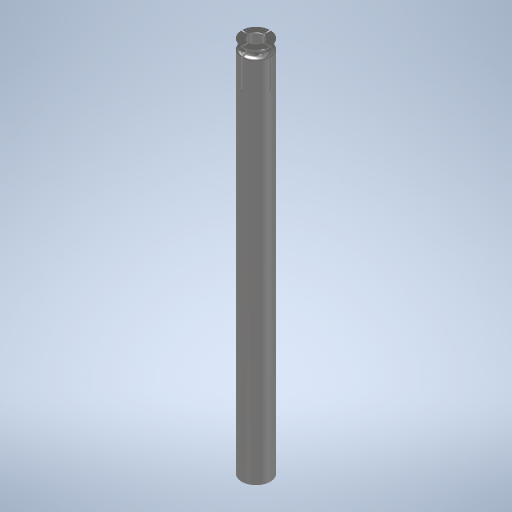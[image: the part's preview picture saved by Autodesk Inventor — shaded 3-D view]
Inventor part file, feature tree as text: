
AUTODESK INVENTOR PART (.ipt)
format: ipt  version: 2023.2 (Build 272271000, 271)  size: 301,056 bytes
history: native  units: mm
features: sketch x6, extrude x5, plane x1, hole x1, chamfer x1, revolve x1
ambient origin geometry x8: Origin, YZ Plane, XZ Plane, XY Plane, X Axis, Y Axis, Z Axis, Center Point
bodies: Volumenkörper1 (feature_tree)
feature tree (15):
  extrude  "Extrusion1"  Depth=6.0mm
  extrude  "Extrusion2"  Depth=8.0mm TaperAngle=0.0deg
  extrude  "Extrusion3"  Depth=3.0mm
  plane  "Arbeitsebene1"
  extrude  "Extrusion4"  Depth=1.0mm TaperAngle=0.0deg
  hole  "Bohrung1"  [1 undecoded]
  chamfer  "Fase1"  Distance=3.0mm
  extrude  "Extrusion5"  Depth=1.0mm
  revolve  "Umdrehung1"
  sketch  "Skizze1"  dims[d0=70.0mm d1=0.0mm d2=6.0mm]
  sketch  "Skizze2"  dims[d3=1.0mm d4=0.0mm d5=8.0mm d6=0.0mm]
  sketch  "Skizze3"  dims[d39=10.0mm d40=10.0mm d9=3.0mm d10=6.0mm d11=4.0mm d12=2.0mm d13=90.0deg d14=23.0mm d15=0.0mm d18=1.5mm]
  sketch  "Skizze4"  dims[d19=1.0mm d20=0.0mm d21=4.0mm d22=0.0mm]
  sketch  "Skizze5"  dims[d25=0.1mm d26=2.0mm d27=45.0deg d28=6.0mm]
  sketch  "Skizze6"  dims[d29=90.0deg d33=3.0mm d34=2.0mm d35=1.0mm d36=6.0mm]
note: 1 required parameter value undecoded (feature->parameter linkage not recoverable at this tier; creation-order binding heuristic only, values carry confidence <= 0.55)
